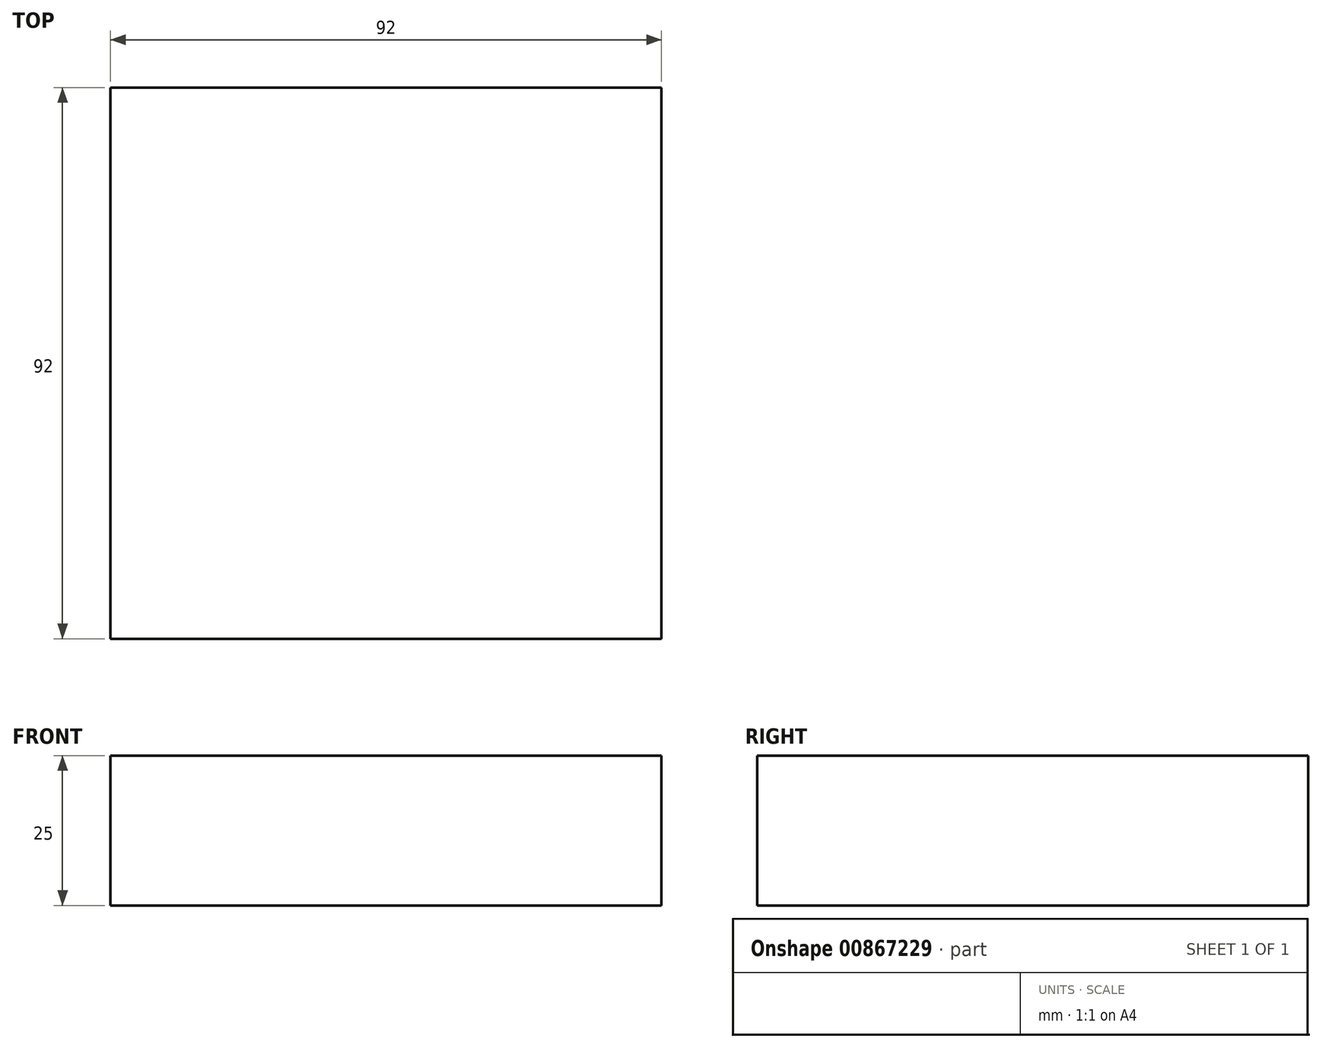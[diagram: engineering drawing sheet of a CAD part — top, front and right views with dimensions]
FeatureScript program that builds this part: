
annotation { "Feature Type Name" : "Feature", "Feature Type Description" : "" }
export const myFeature = defineFeature(function(context is Context, id is Id, definition is map)
    precondition{}
    {
        {
            var Q0;
            Q0=qCreatedBy(makeId("Top.planeOp"),FACE);
            var sketch = newSketch(context, id + "F0", { "sketchPlane" : qUnion([Q0])});
            skLineSegment(sketch, "E0.bottom", {"start": v(-53.91, 56.23) * mm, "end": v(38.09, 56.23) * mm});
            skLineSegment(sketch, "E0.top", {"start": v(-53.91, -35.77) * mm, "end": v(38.09, -35.77) * mm});
            skLineSegment(sketch, "E0.left", {"start": v(-53.91, 56.23) * mm, "end": v(-53.91, -35.77) * mm});
            skLineSegment(sketch, "E0.right", {"start": v(38.09, 56.23) * mm, "end": v(38.09, -35.77) * mm});
            skSolve(sketch);
        }
        {
            var Q0;
            Q0 = qSketchRegion(id + "F0", true);
            extrude(context, id + "F1", {"entities" : qUnion([Q0]), "depth" : 25 * mm, "offsetDistance" : 25.4 * mm});
        }
    });
